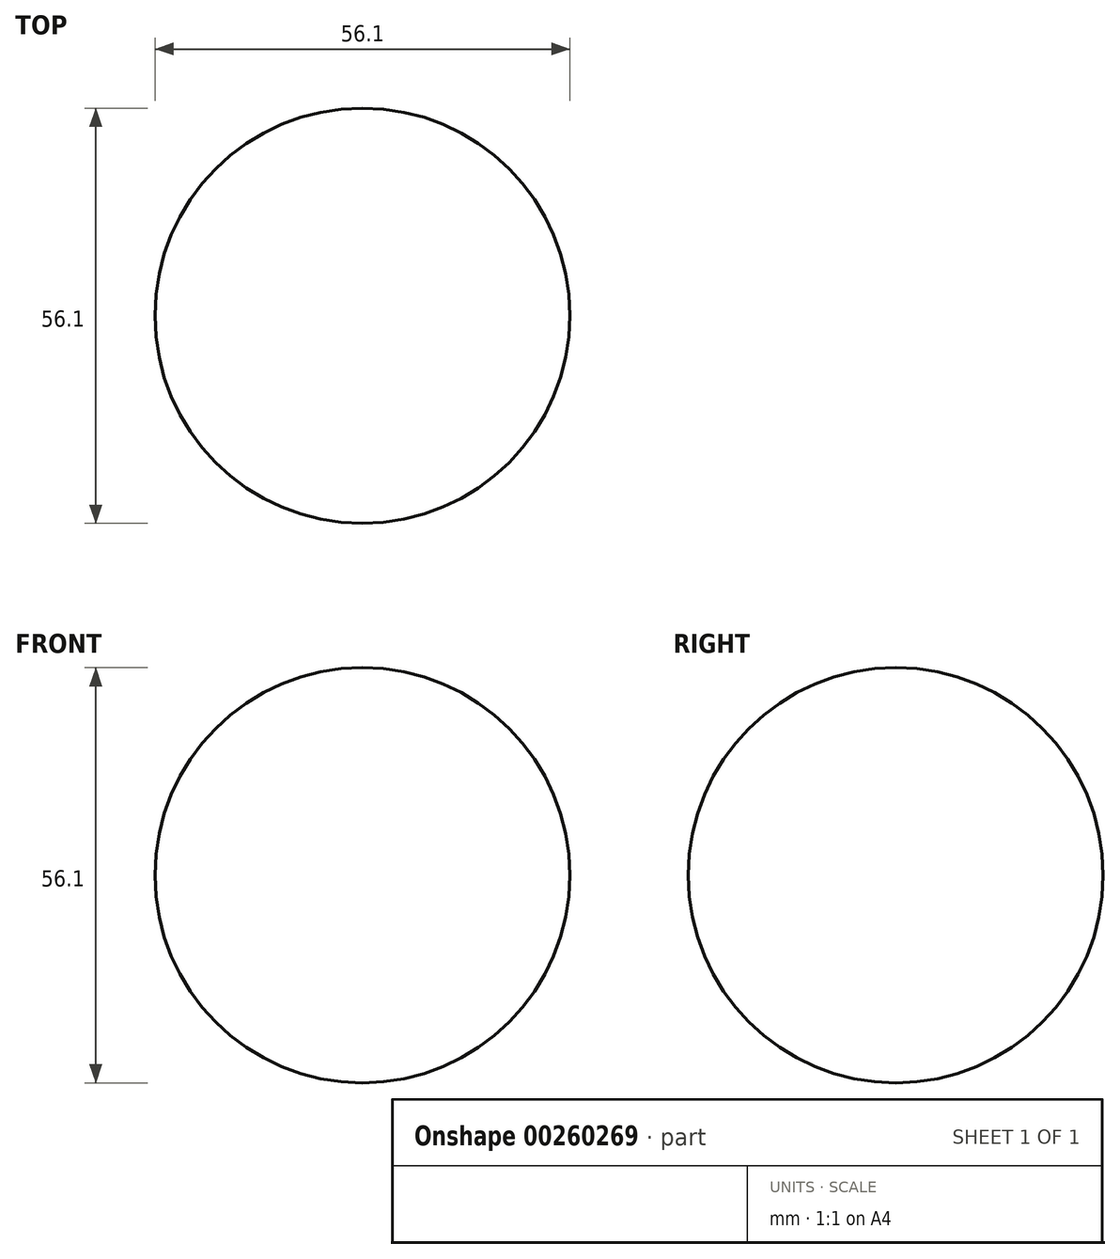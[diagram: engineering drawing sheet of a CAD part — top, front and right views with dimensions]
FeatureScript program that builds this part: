
annotation { "Feature Type Name" : "Feature", "Feature Type Description" : "" }
export const myFeature = defineFeature(function(context is Context, id is Id, definition is map)
    precondition{}
    {
        {
            var Q0;
            Q0=qCreatedBy(makeId("Front.planeOp"),FACE);
            var sketch = newSketch(context, id + "F0", { "sketchPlane" : qUnion([Q0])});
            skArc(sketch, "E0", {"start": v(0, 28.05) * mm, "mid": v(-28.05, 0) * mm, "end": v(0, -28.05) * mm});
            skLineSegment(sketch, "E1", {"start": v(0, 48.23) * mm, "end": v(0, -51.56) * mm, "construction": true});
            skLineSegment(sketch, "E2", {"start": v(0, 28.05) * mm, "end": v(0, -28.05) * mm});
            skSolve(sketch);
        }
        {
            var Q0;
            Q0=makeQuery(id+"F0.imprint","IMPRINT",FACE,{"disambiguationData":[TD([[makeQuery(id+"F0.imprint","IMPRINT",EDGE,{"derivedFrom":sQuery(id+"F0.wireOp",EDGE,"E0")}),1.0]])]});
            var Q1;
            Q1=sQuery(id+"F0.wireOp",EDGE,"E1");
            revolve(context, id + "F1", {"entities" : qUnion([Q0]), "axis" : qUnion([Q1]), "revolveType" : RevolveType.FULL});
        }
    });
